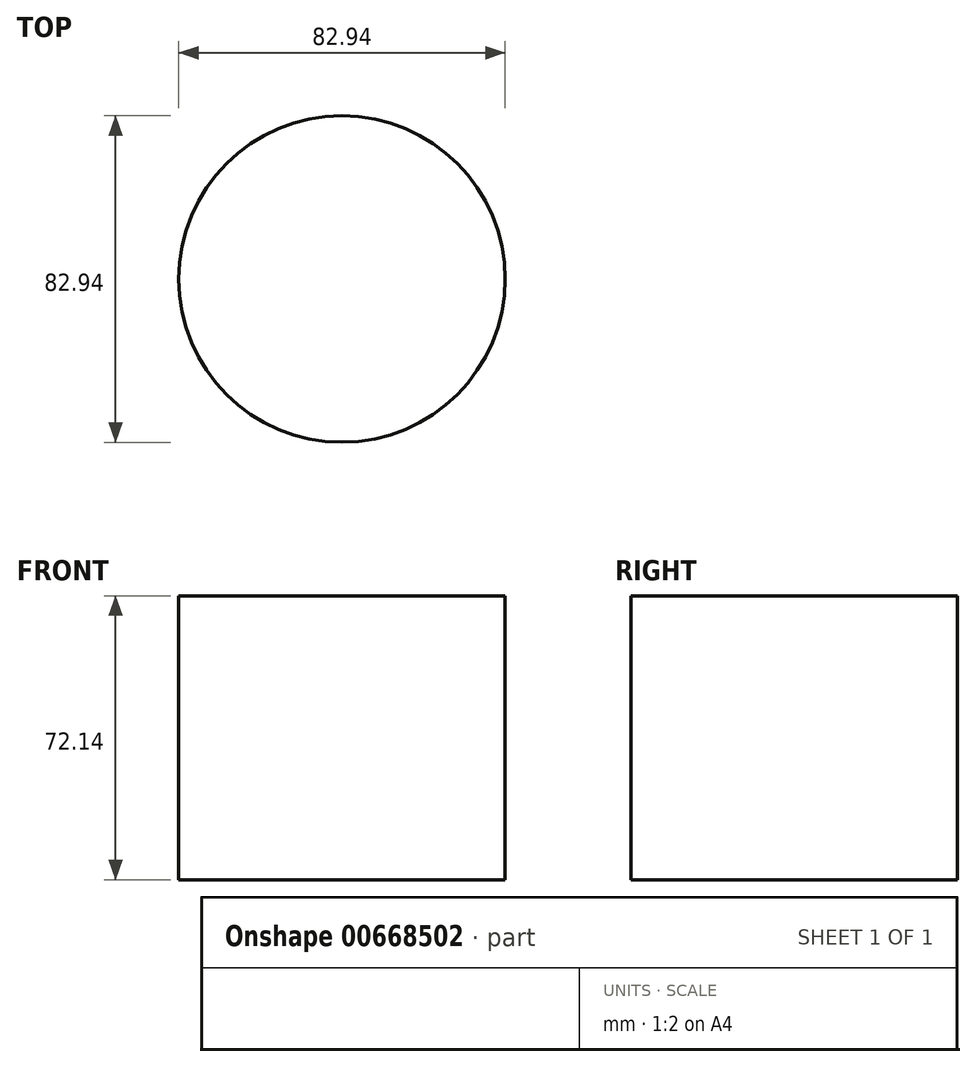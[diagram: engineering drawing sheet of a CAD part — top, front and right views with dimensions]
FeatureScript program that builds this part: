
annotation { "Feature Type Name" : "Feature", "Feature Type Description" : "" }
export const myFeature = defineFeature(function(context is Context, id is Id, definition is map)
    precondition{}
    {
        {
            var Q0;
            Q0=qCreatedBy(makeId("Top.planeOp"),FACE);
            var sketch = newSketch(context, id + "F0", { "sketchPlane" : qUnion([Q0])});
            skCircle(sketch, "E0", {"center": v(0, 0) * mm, "radius": 41.47 * mm});
            skSolve(sketch);
        }
        {
            var Q0;
            Q0 = qSketchRegion(id + "F0", true);
            extrude(context, id + "F1", {"entities" : qUnion([Q0]), "depth" : 72.14 * mm, "offsetDistance" : 25.4 * mm});
        }
    });
